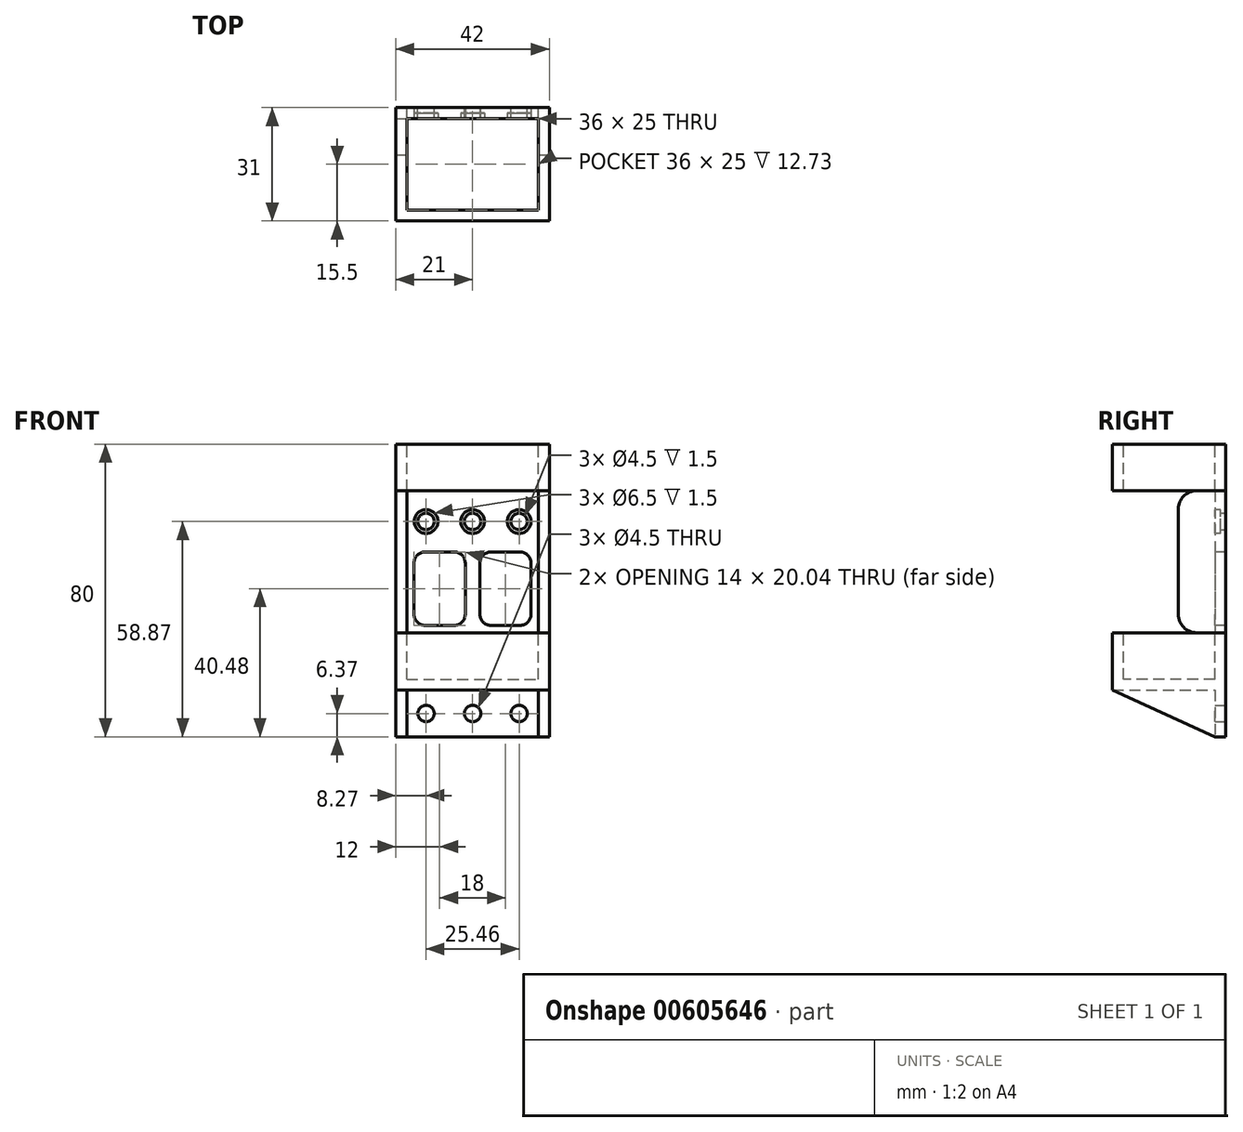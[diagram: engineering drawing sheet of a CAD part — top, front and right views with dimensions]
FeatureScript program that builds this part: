
annotation { "Feature Type Name" : "Feature", "Feature Type Description" : "" }
export const myFeature = defineFeature(function(context is Context, id is Id, definition is map)
    precondition{}
    {
        {
            var Q0;
            Q0=qCreatedBy(makeId("Front.planeOp"),FACE);
            var sketch = newSketch(context, id + "F0", { "sketchPlane" : qUnion([Q0])});
            skLineSegment(sketch, "E0.bottom", {"start": v(0, 0) * mm, "end": v(42, 0) * mm});
            skLineSegment(sketch, "E0.top", {"start": v(0, 80) * mm, "end": v(42, 80) * mm});
            skLineSegment(sketch, "E0.left", {"start": v(0, 0) * mm, "end": v(0, 80) * mm});
            skLineSegment(sketch, "E0.right", {"start": v(42, 0) * mm, "end": v(42, 80) * mm});
            skPoint(sketch, "E1", {"position": v(42, 12.73) * mm});
            skLineSegment(sketch, "E2", {"start": v(42, 12.73) * mm, "end": v(0, 12.73) * mm});
            skPoint(sketch, "E3", {"position": v(3, 12.73) * mm});
            skPoint(sketch, "E4", {"position": v(39, 12.73) * mm});
            skPoint(sketch, "E5", {"position": v(42, 6.37) * mm});
            skPoint(sketch, "E6", {"position": v(21, 6.37) * mm});
            skPoint(sketch, "E6.positionSnap0", {"position": v(21, 0) * mm});
            skCircle(sketch, "E7", {"center": v(21, 6.37) * mm, "radius": 2.25 * mm});
            skPoint(sketch, "E8", {"position": v(33.73, 6.37) * mm});
            skPoint(sketch, "E9", {"position": v(8.27, 6.37) * mm});
            skCircle(sketch, "E10", {"center": v(8.27, 6.37) * mm, "radius": 2.25 * mm});
            skCircle(sketch, "E11", {"center": v(33.73, 6.37) * mm, "radius": 2.25 * mm});
            skPoint(sketch, "E12", {"position": v(42, 15.73) * mm});
            skLineSegment(sketch, "E13", {"start": v(42, 15.73) * mm, "end": v(0, 15.73) * mm});
            skPoint(sketch, "E14", {"position": v(42, 28.46) * mm});
            skLineSegment(sketch, "E15", {"start": v(42, 28.46) * mm, "end": v(0, 28.46) * mm});
            skPoint(sketch, "E16", {"position": v(3, 28.46) * mm});
            skPoint(sketch, "E17", {"position": v(39, 28.46) * mm});
            skLineSegment(sketch, "E18", {"start": v(3, 28.46) * mm, "end": v(3, 15.73) * mm});
            skLineSegment(sketch, "E19", {"start": v(39, 28.46) * mm, "end": v(39, 15.73) * mm});
            skLineSegment(sketch, "E20", {"start": v(3, 12.73) * mm, "end": v(3, 0) * mm});
            skLineSegment(sketch, "E21", {"start": v(39, 12.73) * mm, "end": v(39, 0) * mm});
            skPoint(sketch, "E22", {"position": v(42, 67.27) * mm});
            skLineSegment(sketch, "E23", {"start": v(42, 67.27) * mm, "end": v(0, 67.27) * mm});
            skPoint(sketch, "E24", {"position": v(3, 80) * mm});
            skPoint(sketch, "E25", {"position": v(39, 80) * mm});
            skLineSegment(sketch, "E26", {"start": v(3, 80) * mm, "end": v(3, 67.27) * mm});
            skLineSegment(sketch, "E27", {"start": v(39, 80) * mm, "end": v(39, 67.27) * mm});
            skLineSegment(sketch, "E28", {"start": v(3, 67.27) * mm, "end": v(3, 28.46) * mm});
            skLineSegment(sketch, "E29", {"start": v(39, 67.27) * mm, "end": v(39, 28.46) * mm});
            skPoint(sketch, "E30", {"position": v(21, 58.87) * mm});
            skPoint(sketch, "E31", {"position": v(33.73, 58.87) * mm});
            skPoint(sketch, "E32", {"position": v(8.27, 58.87) * mm});
            skCircle(sketch, "E33", {"center": v(8.27, 58.87) * mm, "radius": 2.25 * mm});
            skCircle(sketch, "E34", {"center": v(21, 58.87) * mm, "radius": 2.25 * mm});
            skCircle(sketch, "E35", {"center": v(33.73, 58.87) * mm, "radius": 2.25 * mm});
            skSolve(sketch);
        }
        {
            var Q0;
            {var subQ0=sQuery(id+"F0.wireOp",EDGE,"E26");Q0=makeQuery(id+"F0.imprint","IMPRINT",FACE,{"disambiguationData":[TD([[makeQuery(id+"F0.imprint","IMPRINT",EDGE,{"derivedFrom":subQ0}),1.0]])]});}
            var Q1;
            {var subQ3=sQuery(id+"F0.wireOp",EDGE,"E26");Q1=makeQuery(id+"F0.imprint","IMPRINT",FACE,{"disambiguationData":[TD([[makeQuery(id+"F0.imprint","IMPRINT",EDGE,{"derivedFrom":subQ3}),-1.0]])]});}
            var Q2;
            {var subQ3=sQuery(id+"F0.wireOp",EDGE,"E27");Q2=makeQuery(id+"F0.imprint","IMPRINT",FACE,{"disambiguationData":[TD([[makeQuery(id+"F0.imprint","IMPRINT",EDGE,{"derivedFrom":subQ3}),1.0]])]});}
            var Q3;
            {var subQ5=sQuery(id+"F0.wireOp",EDGE,"E19");Q3=makeQuery(id+"F0.imprint","IMPRINT",FACE,{"disambiguationData":[TD([[makeQuery(id+"F0.imprint","IMPRINT",EDGE,{"derivedFrom":subQ5}),1.0]])]});}
            var Q4;
            {var subQ0=sQuery(id+"F0.wireOp",EDGE,"E18");Q4=makeQuery(id+"F0.imprint","IMPRINT",FACE,{"disambiguationData":[TD([[makeQuery(id+"F0.imprint","IMPRINT",EDGE,{"derivedFrom":subQ0}),1.0]])]});}
            var Q5;
            {var subQ5=sQuery(id+"F0.wireOp",EDGE,"E18");Q5=makeQuery(id+"F0.imprint","IMPRINT",FACE,{"disambiguationData":[TD([[makeQuery(id+"F0.imprint","IMPRINT",EDGE,{"derivedFrom":subQ5}),-1.0]])]});}
            var Q6;
            {var subQ0=sQuery(id+"F0.wireOp",EDGE,"E2");var subQ9=sQuery(id+"F0.wireOp",EDGE,"E0.left");var subQ10=makeQuery(id+"F0.imprint","INTERSECT",VERTEX,{"derivedFrom":[subQ9,subQ0]});Q6=makeQuery(id+"F0.imprint","IMPRINT",FACE,{"disambiguationData":[TD([[makeQuery(id+"F0.imprint","IMPRINT",EDGE,{"disambiguationData":[TD([[subQ10,-1.0]])],"derivedFrom":subQ9}),-1.0]])]});}
            var Q7;
            Q7=makeQuery(id+"F0.imprint","IMPRINT",FACE,{"disambiguationData":[TD([[makeQuery(id+"F0.imprint","IMPRINT",EDGE,{"derivedFrom":sQuery(id+"F0.wireOp",EDGE,"M8tnBSYo-JXcH-QlTt-2dUG-pDkcxIXN8WWm")}),1.0]])]});
            var Q8;
            Q8=makeQuery(id+"F0.imprint","IMPRINT",FACE,{"disambiguationData":[TD([[makeQuery(id+"F0.imprint","IMPRINT",EDGE,{"derivedFrom":sQuery(id+"F0.wireOp",EDGE,"XjCXGGRX-GFAp-i6Pg-Fx1Q-KsZkCto8yUjJ")}),1.0]])]});
            var Q9;
            Q9=makeQuery(id+"F0.imprint","IMPRINT",FACE,{"disambiguationData":[TD([[makeQuery(id+"F0.imprint","IMPRINT",EDGE,{"derivedFrom":sQuery(id+"F0.wireOp",EDGE,"t6OYUltX-45zE-jHBt-AUaE-XkFXzCzG84Og")}),1.0]])]});
            extrude(context, id + "F1", {"entities" : qUnion([Q0, Q1, Q2, Q3, Q4, Q5, Q6, Q7, Q8, Q9]), "depth" : 31 * mm, "offsetDistance" : 25 * mm});
        }
        {
            var Q0;
            {var subQ5=sQuery(id+"F0.wireOp",EDGE,"E29");Q0=makeQuery(id+"F0.imprint","IMPRINT",FACE,{"disambiguationData":[TD([[makeQuery(id+"F0.imprint","IMPRINT",EDGE,{"derivedFrom":subQ5}),1.0]])]});}
            var Q1;
            {var subQ5=sQuery(id+"F0.wireOp",EDGE,"E28");Q1=makeQuery(id+"F0.imprint","IMPRINT",FACE,{"disambiguationData":[TD([[makeQuery(id+"F0.imprint","IMPRINT",EDGE,{"derivedFrom":subQ5}),-1.0]])]});}
            extrude(context, id + "F2", {"entities" : qUnion([Q0, Q1]), "depth" : 13 * mm, "offsetDistance" : 25 * mm});
        }
        {
            var Q0;
            Q0=makeQuery(id+"F0.imprint","IMPRINT",FACE,{"disambiguationData":[TD([[makeQuery(id+"F0.imprint","IMPRINT",EDGE,{"derivedFrom":sQuery(id+"F0.wireOp",EDGE,"E7")}),-1.0]])]});
            extrude(context, id + "F3", {"entities" : qUnion([Q0]), "operationType" : NewBodyOperationType.ADD, "depth" : 3 * mm, "offsetDistance" : 25 * mm});
        }
        {
            var Q0;
            {var subQ0=sQuery(id+"F0.wireOp",EDGE,"E28");Q0=makeQuery(id+"F0.imprint","IMPRINT",FACE,{"disambiguationData":[TD([[makeQuery(id+"F0.imprint","IMPRINT",EDGE,{"derivedFrom":subQ0}),1.0]])]});}
            extrude(context, id + "F4", {"entities" : qUnion([Q0]), "depth" : 3 * mm, "offsetDistance" : 25 * mm});
        }
        {
            var Q0;
            {var subQ3=sQuery(id+"F0.wireOp",EDGE,"E21");Q0=makeQuery(id+"F0.imprint","IMPRINT",FACE,{"disambiguationData":[TD([[makeQuery(id+"F0.imprint","IMPRINT",EDGE,{"derivedFrom":subQ3}),1.0]])]});}
            var Q1;
            {var subQ3=sQuery(id+"F0.wireOp",EDGE,"E20");Q1=makeQuery(id+"F0.imprint","IMPRINT",FACE,{"disambiguationData":[TD([[makeQuery(id+"F0.imprint","IMPRINT",EDGE,{"derivedFrom":subQ3}),-1.0]])]});}
            extrude(context, id + "F5", {"entities" : qUnion([Q0, Q1]), "operationType" : NewBodyOperationType.ADD, "depth" : 31 * mm, "offsetDistance" : 25 * mm});
        }
        {
            var Q0;
            Q0=makeQuery(id+"F1.opExtrude","SWEPT_FACE",FACE,{"disambiguationData":[OSD([sQuery(id+"F0.wireOp",EDGE,"E15")])]});
            var sketch = newSketch(context, id + "F6", { "sketchPlane" : qUnion([Q0])});
            skPoint(sketch, "E36", {"position": v(42, -28) * mm});
            skPoint(sketch, "E37", {"position": v(39, -31) * mm});
            skPoint(sketch, "E38", {"position": v(39, -28) * mm});
            skPoint(sketch, "E39", {"position": v(0, -3) * mm});
            skPoint(sketch, "E40", {"position": v(3, 0) * mm});
            skPoint(sketch, "E41", {"position": v(3, -3) * mm});
            skLineSegment(sketch, "E42.bottom", {"start": v(3, -3) * mm, "end": v(39, -3) * mm});
            skLineSegment(sketch, "E42.top", {"start": v(3, -28) * mm, "end": v(39, -28) * mm});
            skLineSegment(sketch, "E42.left", {"start": v(3, -3) * mm, "end": v(3, -28) * mm});
            skLineSegment(sketch, "E42.right", {"start": v(39, -3) * mm, "end": v(39, -28) * mm});
            skSolve(sketch);
        }
        {
            var Q0;
            Q0=makeQuery(id+"F6.imprint","IMPRINT",FACE,{"disambiguationData":[TD([[makeQuery(id+"F6.imprint","IMPRINT",EDGE,{"derivedFrom":sQuery(id+"F6.wireOp",EDGE,"E42.bottom")}),-1.0]])]});
            extrude(context, id + "F7", {"entities" : qUnion([Q0]), "operationType" : NewBodyOperationType.REMOVE, "oppositeDirection" : true, "depth" : 12.73 * mm, "offsetDistance" : 25 * mm});
        }
        {
            var Q0;
            Q0=makeQuery(id+"F1.opExtrude","SWEPT_FACE",FACE,{"disambiguationData":[OSD([sQuery(id+"F0.wireOp",EDGE,"E0.top")])]});
            var sketch = newSketch(context, id + "F8", { "sketchPlane" : qUnion([Q0])});
            skPoint(sketch, "E43", {"position": v(0, -3) * mm});
            skPoint(sketch, "E44", {"position": v(3, 0) * mm});
            skPoint(sketch, "E45", {"position": v(39, -31) * mm});
            skPoint(sketch, "E46", {"position": v(42, -28) * mm});
            skPoint(sketch, "E47", {"position": v(3, -3) * mm});
            skPoint(sketch, "E48", {"position": v(39, -28) * mm});
            skLineSegment(sketch, "E49.bottom", {"start": v(3, -3) * mm, "end": v(39, -3) * mm});
            skLineSegment(sketch, "E49.top", {"start": v(3, -28) * mm, "end": v(39, -28) * mm});
            skLineSegment(sketch, "E49.left", {"start": v(3, -3) * mm, "end": v(3, -28) * mm});
            skLineSegment(sketch, "E49.right", {"start": v(39, -3) * mm, "end": v(39, -28) * mm});
            skSolve(sketch);
        }
        {
            var Q0;
            Q0=makeQuery(id+"F8.imprint","IMPRINT",FACE,{"disambiguationData":[TD([[makeQuery(id+"F8.imprint","IMPRINT",EDGE,{"derivedFrom":sQuery(id+"F8.wireOp",EDGE,"E49.bottom")}),-1.0]])]});
            extrude(context, id + "F9", {"entities" : qUnion([Q0]), "operationType" : NewBodyOperationType.REMOVE, "oppositeDirection" : true, "depth" : 25 * mm, "offsetDistance" : 25 * mm});
        }
        {
            var Q0;
            Q0=makeQuery(id+"F5.opExtrude","SWEPT_FACE",FACE,{"disambiguationData":[OSD([sQuery(id+"F0.wireOp",EDGE,"E20")])]});
            var sketch = newSketch(context, id + "F10", { "sketchPlane" : qUnion([Q0])});
            skLineSegment(sketch, "E50", {"start": v(-31, 12.73) * mm, "end": v(-3, 0) * mm});
            skSolve(sketch);
        }
        {
            var Q0;
            Q0=makeQuery(id+"F10.imprint","IMPRINT",FACE,{"disambiguationData":[TD([[makeQuery(id+"F10.imprint","IMPRINT",EDGE,{"derivedFrom":sQuery(id+"F10.wireOp",EDGE,"E50")}),-1.0]])]});
            extrude(context, id + "F11", {"entities" : qUnion([Q0]), "operationType" : NewBodyOperationType.REMOVE, "oppositeDirection" : true, "depth" : 25 * mm, "offsetDistance" : 25 * mm});
        }
        {
            var Q0;
            Q0=makeQuery(id+"F5.opExtrude","SWEPT_FACE",FACE,{"disambiguationData":[OSD([sQuery(id+"F0.wireOp",EDGE,"E21")])]});
            var sketch = newSketch(context, id + "F12", { "sketchPlane" : qUnion([Q0])});
            skLineSegment(sketch, "E51", {"start": v(31, 12.73) * mm, "end": v(3, 0) * mm});
            skSolve(sketch);
        }
        {
            var Q0;
            Q0=makeQuery(id+"F12.imprint","IMPRINT",FACE,{"disambiguationData":[TD([[makeQuery(id+"F12.imprint","IMPRINT",EDGE,{"derivedFrom":sQuery(id+"F12.wireOp",EDGE,"E51")}),1.0]])]});
            extrude(context, id + "F13", {"entities" : qUnion([Q0]), "operationType" : NewBodyOperationType.REMOVE, "oppositeDirection" : true, "depth" : 25 * mm, "offsetDistance" : 25 * mm});
        }
        {
            var Q0;
            Q0=makeQuery(id+"F4.opExtrude","CAP_FACE",FACE,{"disambiguationData":[OSD([sQuery(id+"F0.wireOp",EDGE,"E15"),sQuery(id+"F0.wireOp",EDGE,"E23"),sQuery(id+"F0.wireOp",EDGE,"E28"),sQuery(id+"F0.wireOp",EDGE,"E29"),sQuery(id+"F0.wireOp",EDGE,"E33"),sQuery(id+"F0.wireOp",EDGE,"E34"),sQuery(id+"F0.wireOp",EDGE,"E35")])],"isStart":false});
            var sketch = newSketch(context, id + "F14", { "sketchPlane" : qUnion([Q0])});
            skCircle(sketch, "E52", {"center": v(8.27, 58.87) * mm, "radius": 3.25 * mm});
            skCircle(sketch, "E53", {"center": v(21, 58.87) * mm, "radius": 3.25 * mm});
            skCircle(sketch, "E54", {"center": v(33.73, 58.87) * mm, "radius": 3.25 * mm});
            skSolve(sketch);
        }
        {
            var Q0;
            Q0=makeQuery(id+"F14.imprint","IMPRINT",FACE,{"disambiguationData":[TD([[makeQuery(id+"F14.imprint","IMPRINT",EDGE,{"derivedFrom":sQuery(id+"F14.wireOp",EDGE,"E52")}),1.0]])]});
            var Q1;
            Q1=makeQuery(id+"F14.imprint","IMPRINT",FACE,{"disambiguationData":[TD([[makeQuery(id+"F14.imprint","IMPRINT",EDGE,{"derivedFrom":sQuery(id+"F14.wireOp",EDGE,"E53")}),1.0]])]});
            var Q2;
            Q2=makeQuery(id+"F14.imprint","IMPRINT",FACE,{"disambiguationData":[TD([[makeQuery(id+"F14.imprint","IMPRINT",EDGE,{"derivedFrom":sQuery(id+"F14.wireOp",EDGE,"E54")}),1.0]])]});
            extrude(context, id + "F15", {"entities" : qUnion([Q0, Q1, Q2]), "operationType" : NewBodyOperationType.REMOVE, "oppositeDirection" : true, "depth" : 1.5 * mm, "offsetDistance" : 25 * mm});
        }
        {
            var Q0;
            Q0=makeQuery(id+"F4.opExtrude","CAP_FACE",FACE,{"disambiguationData":[OSD([sQuery(id+"F0.wireOp",EDGE,"E15"),sQuery(id+"F0.wireOp",EDGE,"E23"),sQuery(id+"F0.wireOp",EDGE,"E28"),sQuery(id+"F0.wireOp",EDGE,"E29"),sQuery(id+"F0.wireOp",EDGE,"E33"),sQuery(id+"F0.wireOp",EDGE,"E34"),sQuery(id+"F0.wireOp",EDGE,"E35")])],"isStart":false});
            var sketch = newSketch(context, id + "F16", { "sketchPlane" : qUnion([Q0])});
            skLineSegment(sketch, "E55", {"start": v(21, 58.87) * mm, "end": v(21, 52.5) * mm, "construction": true});
            skLineSegment(sketch, "E56", {"start": v(21, 52.5) * mm, "end": v(39, 52.5) * mm});
            skLineSegment(sketch, "E57", {"start": v(21, 52.5) * mm, "end": v(21, 28.46) * mm});
            skPoint(sketch, "E58", {"position": v(3, 52.5) * mm});
            skPoint(sketch, "E59", {"position": v(39, 52.5) * mm});
            skLineSegment(sketch, "E60", {"start": v(39, 52.5) * mm, "end": v(39, 28.46) * mm});
            skLineSegment(sketch, "E61", {"start": v(39, 28.46) * mm, "end": v(21, 28.46) * mm});
            skLineSegment(sketch, "E62", {"start": v(3, 52.5) * mm, "end": v(3, 28.46) * mm});
            skPoint(sketch, "E63", {"position": v(21, 52.5) * mm});
            skPoint(sketch, "E64", {"position": v(21, 28.46) * mm});
            skLineSegment(sketch, "E65", {"start": v(21, 28.46) * mm, "end": v(3, 28.46) * mm});
            skLineSegment(sketch, "E66", {"start": v(3, 52.5) * mm, "end": v(21, 52.5) * mm});
            skLineSegment(sketch, "E67.0", {"start": v(23, 50.5) * mm, "end": v(37, 50.5) * mm});
            skLineSegment(sketch, "E67.1", {"start": v(23, 50.5) * mm, "end": v(23, 30.46) * mm});
            skLineSegment(sketch, "E67.2", {"start": v(37, 30.46) * mm, "end": v(23, 30.46) * mm});
            skLineSegment(sketch, "E67.3", {"start": v(37, 50.5) * mm, "end": v(37, 30.46) * mm});
            skLineSegment(sketch, "E68.0", {"start": v(5, 50.5) * mm, "end": v(19, 50.5) * mm});
            skLineSegment(sketch, "E68.1", {"start": v(5, 50.5) * mm, "end": v(5, 30.46) * mm});
            skLineSegment(sketch, "E68.2", {"start": v(19, 30.46) * mm, "end": v(5, 30.46) * mm});
            skLineSegment(sketch, "E68.3", {"start": v(19, 50.5) * mm, "end": v(19, 30.46) * mm});
            skSolve(sketch);
        }
        {
            var Q0;
            Q0=makeQuery(id+"F16.imprint","IMPRINT",FACE,{"disambiguationData":[TD([[makeQuery(id+"F16.imprint","IMPRINT",EDGE,{"derivedFrom":sQuery(id+"F16.wireOp",EDGE,"E68.0")}),-1.0]])]});
            var Q1;
            Q1=makeQuery(id+"F16.imprint","IMPRINT",FACE,{"disambiguationData":[TD([[makeQuery(id+"F16.imprint","IMPRINT",EDGE,{"derivedFrom":sQuery(id+"F16.wireOp",EDGE,"E67.0")}),-1.0]])]});
            extrude(context, id + "F17", {"entities" : qUnion([Q0, Q1]), "operationType" : NewBodyOperationType.REMOVE, "oppositeDirection" : true, "depth" : 25 * mm, "offsetDistance" : 25 * mm});
        }
        {
            var Q0;
            Q0=makeQuery(id+"F17.boolean.opBoolean","COPY",EDGE,{"derivedFrom":makeQuery(id+"F17.opExtrude","SWEPT_EDGE",EDGE,{"disambiguationData":[OSD([sQuery(id+"F16.wireOp",EDGE,"E68.0"),sQuery(id+"F16.wireOp",EDGE,"E68.1")])]})});
            var Q1;
            Q1=makeQuery(id+"F17.boolean.opBoolean","COPY",EDGE,{"derivedFrom":makeQuery(id+"F17.opExtrude","SWEPT_EDGE",EDGE,{"disambiguationData":[OSD([sQuery(id+"F16.wireOp",EDGE,"E68.1"),sQuery(id+"F16.wireOp",EDGE,"E68.2")])]})});
            var Q2;
            Q2=makeQuery(id+"F17.boolean.opBoolean","COPY",EDGE,{"derivedFrom":makeQuery(id+"F17.opExtrude","SWEPT_EDGE",EDGE,{"disambiguationData":[OSD([sQuery(id+"F16.wireOp",EDGE,"E67.2"),sQuery(id+"F16.wireOp",EDGE,"E67.3")])]})});
            var Q3;
            Q3=makeQuery(id+"F17.boolean.opBoolean","COPY",EDGE,{"derivedFrom":makeQuery(id+"F17.opExtrude","SWEPT_EDGE",EDGE,{"disambiguationData":[OSD([sQuery(id+"F16.wireOp",EDGE,"E67.1"),sQuery(id+"F16.wireOp",EDGE,"E67.2")])]})});
            var Q4;
            Q4=makeQuery(id+"F17.boolean.opBoolean","COPY",EDGE,{"derivedFrom":makeQuery(id+"F17.opExtrude","SWEPT_EDGE",EDGE,{"disambiguationData":[OSD([sQuery(id+"F16.wireOp",EDGE,"E68.2"),sQuery(id+"F16.wireOp",EDGE,"E68.3")])]})});
            var Q5;
            Q5=makeQuery(id+"F17.boolean.opBoolean","COPY",EDGE,{"derivedFrom":makeQuery(id+"F17.opExtrude","SWEPT_EDGE",EDGE,{"disambiguationData":[OSD([sQuery(id+"F16.wireOp",EDGE,"E68.0"),sQuery(id+"F16.wireOp",EDGE,"E68.3")])]})});
            var Q6;
            Q6=makeQuery(id+"F17.boolean.opBoolean","COPY",EDGE,{"derivedFrom":makeQuery(id+"F17.opExtrude","SWEPT_EDGE",EDGE,{"disambiguationData":[OSD([sQuery(id+"F16.wireOp",EDGE,"E67.0"),sQuery(id+"F16.wireOp",EDGE,"E67.1")])]})});
            var Q7;
            Q7=makeQuery(id+"F17.boolean.opBoolean","COPY",EDGE,{"derivedFrom":makeQuery(id+"F17.opExtrude","SWEPT_EDGE",EDGE,{"disambiguationData":[OSD([sQuery(id+"F16.wireOp",EDGE,"E67.0"),sQuery(id+"F16.wireOp",EDGE,"E67.3")])]})});
            fillet(context, id + "F18", {"entities" : qUnion([Q0, Q1, Q2, Q3, Q4, Q5, Q6, Q7]), "radius" : 3 * mm, "tangentPropagation" : true, "allowEdgeOverflow" : false});
        }
        {
            var Q0;
            {var subQ0=sQuery(id+"F0.wireOp",EDGE,"E23");Q0=makeQuery(id+"F2.opExtrude","CAP_EDGE",EDGE,{"disambiguationData":[OSD([subQ0]),TDD([makeQuery(id+"F0.imprint","IMPRINT",EDGE,{"disambiguationData":[TD([[makeQuery(id+"F0.imprint","INTERSECT",VERTEX,{"derivedFrom":[sQuery(id+"F0.wireOp",EDGE,"E0.left"),subQ0]}),1.0]])],"derivedFrom":subQ0})])],"isStart":false});}
            var Q1;
            {var subQ0=sQuery(id+"F0.wireOp",EDGE,"E23");Q1=makeQuery(id+"F2.opExtrude","CAP_EDGE",EDGE,{"disambiguationData":[OSD([subQ0]),TDD([makeQuery(id+"F0.imprint","IMPRINT",EDGE,{"disambiguationData":[TD([[makeQuery(id+"F0.imprint","INTERSECT",VERTEX,{"derivedFrom":[sQuery(id+"F0.wireOp",EDGE,"E0.right"),subQ0]}),-1.0]])],"derivedFrom":subQ0})])],"isStart":false});}
            var Q2;
            {var subQ0=sQuery(id+"F0.wireOp",EDGE,"E15");Q2=makeQuery(id+"F2.opExtrude","CAP_EDGE",EDGE,{"disambiguationData":[OSD([subQ0]),TDD([makeQuery(id+"F0.imprint","IMPRINT",EDGE,{"disambiguationData":[TD([[makeQuery(id+"F0.imprint","INTERSECT",VERTEX,{"derivedFrom":[sQuery(id+"F0.wireOp",EDGE,"E0.left"),subQ0]}),1.0]])],"derivedFrom":subQ0})])],"isStart":false});}
            var Q3;
            {var subQ0=sQuery(id+"F0.wireOp",EDGE,"E15");Q3=makeQuery(id+"F2.opExtrude","CAP_EDGE",EDGE,{"disambiguationData":[OSD([subQ0]),TDD([makeQuery(id+"F0.imprint","IMPRINT",EDGE,{"disambiguationData":[TD([[makeQuery(id+"F0.imprint","INTERSECT",VERTEX,{"derivedFrom":[sQuery(id+"F0.wireOp",EDGE,"E0.right"),subQ0]}),-1.0]])],"derivedFrom":subQ0})])],"isStart":false});}
            fillet(context, id + "F19", {"entities" : qUnion([Q0, Q1, Q2, Q3]), "radius" : 5 * mm, "tangentPropagation" : true, "allowEdgeOverflow" : false});
        }
    });
